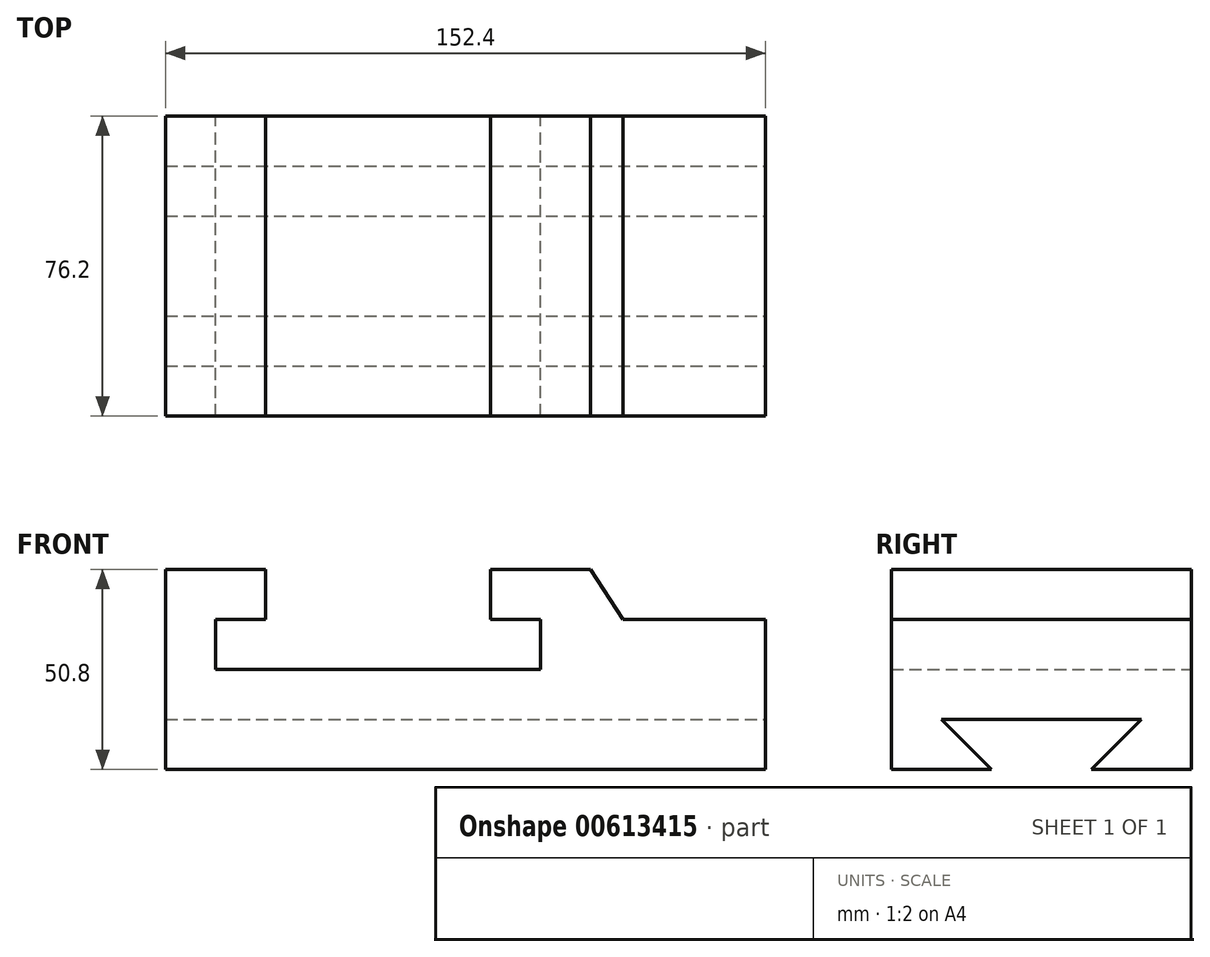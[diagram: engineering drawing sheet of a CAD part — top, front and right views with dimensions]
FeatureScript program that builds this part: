
annotation { "Feature Type Name" : "Feature", "Feature Type Description" : "" }
export const myFeature = defineFeature(function(context is Context, id is Id, definition is map)
    precondition{}
    {
        {
            var Q0;
            Q0=qCreatedBy(makeId("Front.planeOp"),FACE);
            var sketch = newSketch(context, id + "F0", { "sketchPlane" : qUnion([Q0])});
            skLineSegment(sketch, "E0", {"start": v(0, 0) * mm, "end": v(0, 50.8) * mm});
            skLineSegment(sketch, "E1", {"start": v(0, 0) * mm, "end": v(152.4, 0) * mm});
            skLineSegment(sketch, "E2", {"start": v(152.4, 0) * mm, "end": v(152.4, 38.1) * mm});
            skLineSegment(sketch, "E3", {"start": v(0, 50.8) * mm, "end": v(25.4, 50.8) * mm});
            skLineSegment(sketch, "E4", {"start": v(25.4, 50.8) * mm, "end": v(25.4, 38.1) * mm});
            skLineSegment(sketch, "E5", {"start": v(25.4, 38.1) * mm, "end": v(12.7, 38.1) * mm});
            skLineSegment(sketch, "E6", {"start": v(12.7, 38.1) * mm, "end": v(12.7, 25.4) * mm});
            skLineSegment(sketch, "E7", {"start": v(82.55, 25.4) * mm, "end": v(95.25, 25.4) * mm});
            skLineSegment(sketch, "E8", {"start": v(82.55, 38.1) * mm, "end": v(82.55, 50.8) * mm});
            skPoint(sketch, "E8.endSnap0", {"position": v(12.7, 50.8) * mm});
            skLineSegment(sketch, "E9", {"start": v(82.55, 50.8) * mm, "end": v(107.95, 50.8) * mm});
            skLineSegment(sketch, "E10", {"start": v(12.7, 25.4) * mm, "end": v(82.55, 25.4) * mm});
            skLineSegment(sketch, "E11", {"start": v(82.55, 38.1) * mm, "end": v(95.25, 38.1) * mm});
            skLineSegment(sketch, "E12", {"start": v(95.25, 38.1) * mm, "end": v(95.25, 25.4) * mm});
            skLineSegment(sketch, "E13", {"start": v(107.95, 50.8) * mm, "end": v(116.14, 38.1) * mm});
            skLineSegment(sketch, "E14", {"start": v(116.14, 38.1) * mm, "end": v(152.4, 38.1) * mm});
            skSolve(sketch);
        }
        {
            var Q0;
            Q0 = qSketchRegion(id + "F0", true);
            extrude(context, id + "F1", {"entities" : qUnion([Q0]), "depth" : 76.2 * mm, "offsetDistance" : 25.4 * mm});
        }
        {
            var Q0;
            Q0=makeQuery(id+"F1.opExtrude","SWEPT_FACE",FACE,{"disambiguationData":[OSD([sQuery(id+"F0.wireOp",EDGE,"E2")])]});
            var sketch = newSketch(context, id + "F2", { "sketchPlane" : qUnion([Q0])});
            skPoint(sketch, "E15", {"position": v(-38.1, 0) * mm});
            skLineSegment(sketch, "E16", {"start": v(-38.1, 12.7) * mm, "end": v(-63.5, 12.7) * mm});
            skLineSegment(sketch, "E17", {"start": v(-38.1, 12.7) * mm, "end": v(-12.7, 12.7) * mm});
            skLineSegment(sketch, "E18", {"start": v(-63.5, 12.7) * mm, "end": v(-50.8, 0) * mm});
            skLineSegment(sketch, "E19", {"start": v(-12.7, 12.7) * mm, "end": v(-25.4, 0) * mm});
            skLineSegment(sketch, "E20", {"start": v(-50.8, 0) * mm, "end": v(-25.4, 0) * mm});
            skSolve(sketch);
        }
        {
            var Q0;
            Q0=makeQuery(id+"F2.imprint","IMPRINT",FACE,{"disambiguationData":[TD([[makeQuery(id+"F2.imprint","IMPRINT",EDGE,{"derivedFrom":sQuery(id+"F2.wireOp",EDGE,"E16")}),1.0]])]});
            extrude(context, id + "F3", {"entities" : qUnion([Q0]), "operationType" : NewBodyOperationType.REMOVE, "oppositeDirection" : true, "depth" : 152.4 * mm, "offsetDistance" : 25.4 * mm});
        }
    });
